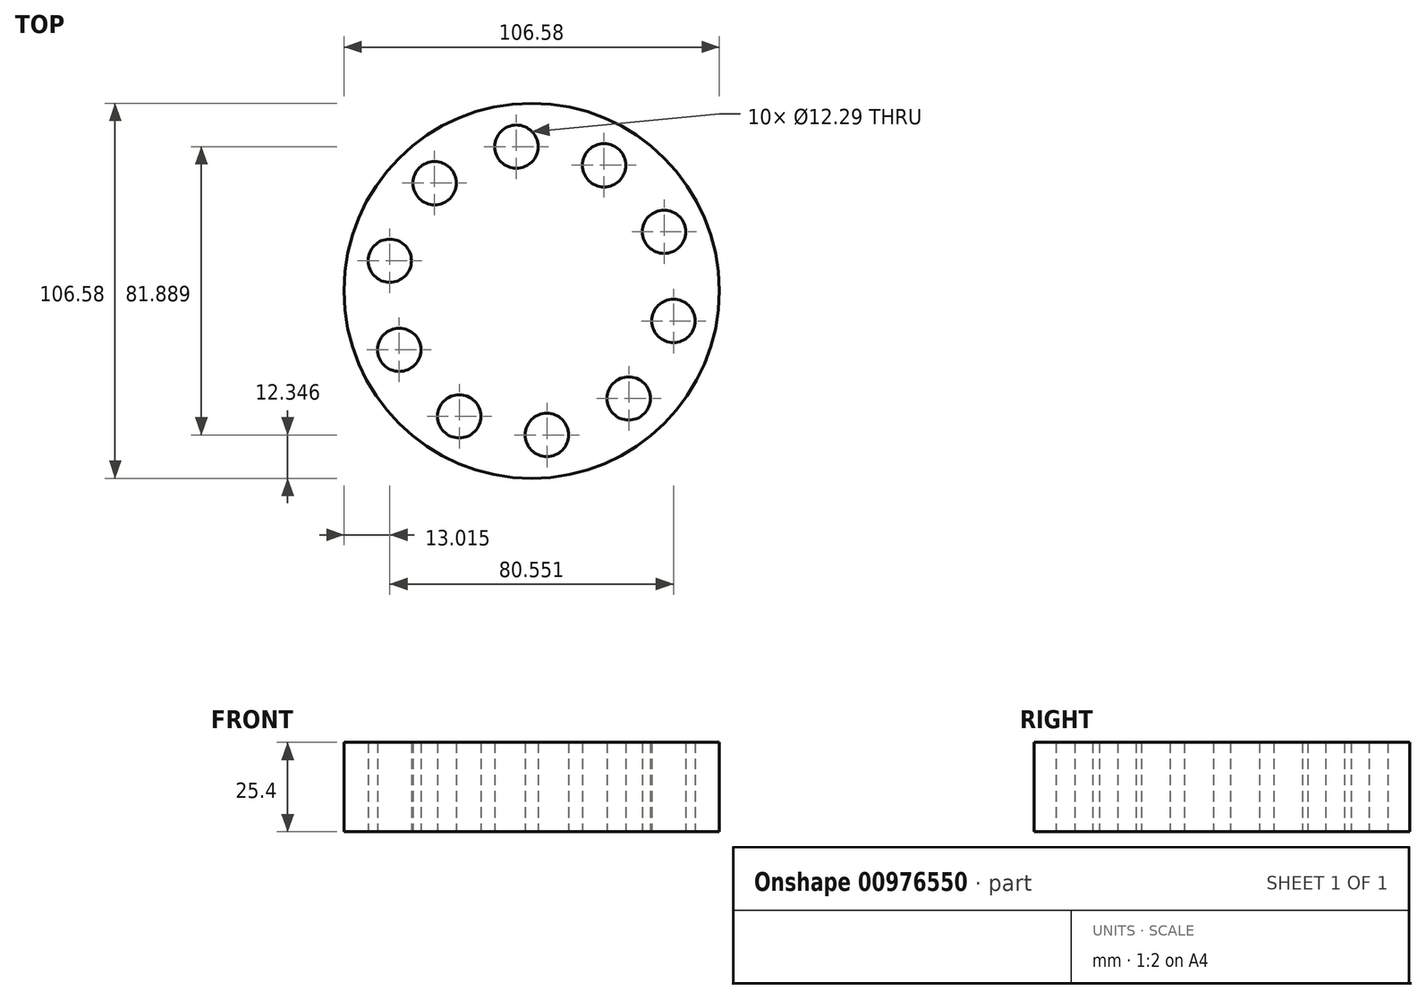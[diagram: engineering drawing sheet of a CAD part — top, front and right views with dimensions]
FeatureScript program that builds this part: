
annotation { "Feature Type Name" : "Feature", "Feature Type Description" : "" }
export const myFeature = defineFeature(function(context is Context, id is Id, definition is map)
    precondition{}
    {
        {
            var Q0;
            Q0=qCreatedBy(makeId("Top.planeOp"),FACE);
            var sketch = newSketch(context, id + "F0", { "sketchPlane" : qUnion([Q0])});
            skCircle(sketch, "E0", {"center": v(0, 0) * mm, "radius": 53.3 * mm});
            skCircle(sketch, "E1", {"center": v(-27.56, 30.59) * mm, "radius": 6.14 * mm});
            skCircle(sketch, "E2.1.0", {"center": v(-40.28, 8.54) * mm, "radius": 6.14 * mm});
            skCircle(sketch, "E2.2.0", {"center": v(-37.6, -16.76) * mm, "radius": 6.14 * mm});
            skCircle(sketch, "E2.3.0", {"center": v(-20.57, -35.66) * mm, "radius": 6.14 * mm});
            skCircle(sketch, "E2.4.0", {"center": v(4.32, -40.94) * mm, "radius": 6.14 * mm});
            skCircle(sketch, "E2.5.0", {"center": v(27.56, -30.59) * mm, "radius": 6.14 * mm});
            skCircle(sketch, "E2.6.0", {"center": v(40.28, -8.54) * mm, "radius": 6.14 * mm});
            skCircle(sketch, "E2.7.0", {"center": v(37.6, 16.76) * mm, "radius": 6.14 * mm});
            skCircle(sketch, "E2.8.0", {"center": v(20.57, 35.66) * mm, "radius": 6.14 * mm});
            skCircle(sketch, "E2.9.0", {"center": v(-4.32, 40.94) * mm, "radius": 6.14 * mm});
            skSolve(sketch);
        }
        {
            var Q0;
            Q0 = qSketchRegion(id + "F0", true);
            extrude(context, id + "F1", {"entities" : qUnion([Q0]), "depth" : 25.4 * mm, "offsetDistance" : 25.4 * mm, "symmetric" : true});
        }
    });
